# Revit family: Kessel AG 93002.00D1R en
name_source: partatom
category: Sanitärinstallationen
revit_build: Autodesk Revit 2014 (Build: 20130308_1515(x64)
units: mm (PartAtom-declared; Revit-internal decimal feet)

## types (1)
- Kessel AG 93002.00D1R en
    <1.010.00.2> Number of the part of the guideline = 99
    <1.010.00.3> Issue date (month) of the guideline = 200601
    <1.010.00.4> Manufacturer name = Kessel AG
    <1.010.00.5> Revision date of the file = Kessel AG
    <1.100.00.3> Sort number for display sequence = 1
    <1.100.00.4> Product designation = Abscheideranlage für Fette
    <1.110.00.3> Sort number for display sequence = 1
    <1.110.00.4> Product designation = Fettabscheider EasyClean Modular
    <1.110.00.5> Product main group = EasyClean modular grease separator
    <1.800.00.3> BS number = 001002000001005008008006012001002002005???00400021???
    <1.800.00.4> Comment field = Fettabscheider EasyClean Modular NS 2, Direct, 2-teilig
    <1.810.00.3> Manufacturer’s reference number = 93002.00/D1-R
    <1.810.00.4> DATANORM number = 93002.00/D1-R
    <99.200.00.3> Product name = Freiaufstellung
    <99.250.00.3> Length [mm] = Direct
    <99.260.00.3> Width [mm] = 200
    <99.300.00.3> Height [mm] = 400
    <99.350.00.3> Weight [kg] = 100
    <99.360.00.3> certification identifications = 600
    <99.400.00.3> Driving = nein
    <99.450.00.3> Attraction Nominal / operating voltage of the regulator = 100
    <99.460.00.3> Output Voltage [V] = 100
    <99.500.00.3> standardized bus protocols = 2
    <99.700.00.4> Product property = Fettabscheider EasyClean Modular NS 2, Direct, 2-teilig
    CONNECTOR0_DIAMETER_dX_0r = 0 mm  [stored 0 ft]
    CONNECTOR0_dX_00 = 545 mm
    CONNECTOR0_dX_01 = 435 mm
    CONNECTOR0_ref_dX = 435 mm
    CONNECTOR0_ref_dZ = 1143 mm
    CONNECTOR1_DIAMETER_dX_0r = 0 mm  [stored 0 ft]
    CONNECTOR1_dX_00 = 435 mm
    CONNECTOR1_dX_01 = 545 mm
    CONNECTOR1_ref_dX = 435 mm
    CONNECTOR1_ref_dZ = 1073 mm
    CONNECTOR2_DIAMETER_dZ_0r = 0 mm  [stored 0 ft]
    CONNECTOR2_dZ_00 = 1110 mm
    CONNECTOR2_dZ_01 = 1160 mm
    CONNECTOR2_ref_dX = 429 mm
    CONNECTOR2_ref_dY = 429 mm
    CONNECTOR2_ref_dZ = 1110 mm
    Hersteller = Kessel AG
    Modell = 93002.00/D1-R

note: [stored X ft] marks values corroborated as IEEE doubles in the binary element streams (Revit-internal decimal feet)
